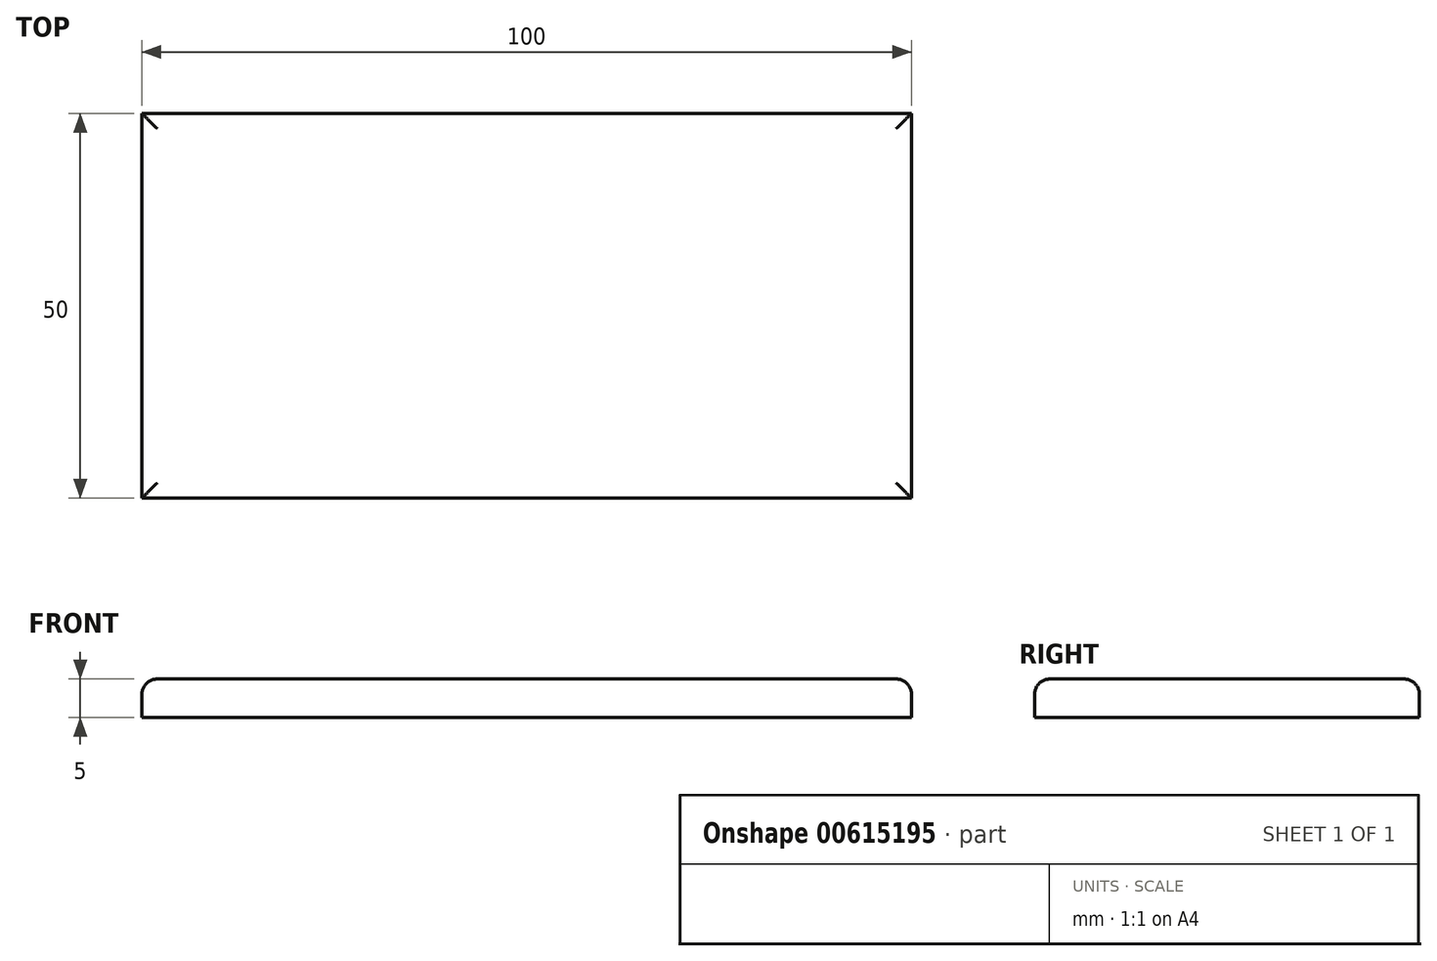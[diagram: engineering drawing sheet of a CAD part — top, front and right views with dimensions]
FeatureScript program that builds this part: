
annotation { "Feature Type Name" : "Feature", "Feature Type Description" : "" }
export const myFeature = defineFeature(function(context is Context, id is Id, definition is map)
    precondition{}
    {
        {
            var Q0;
            Q0=qCreatedBy(makeId("Top.planeOp"),FACE);
            var sketch = newSketch(context, id + "F0", { "sketchPlane" : qUnion([Q0])});
            skLineSegment(sketch, "E0.bottom", {"start": v(0, 0) * mm, "end": v(100, 0) * mm});
            skLineSegment(sketch, "E0.top", {"start": v(0, 50) * mm, "end": v(100, 50) * mm});
            skLineSegment(sketch, "E0.left", {"start": v(0, 0) * mm, "end": v(0, 50) * mm});
            skLineSegment(sketch, "E0.right", {"start": v(100, 0) * mm, "end": v(100, 50) * mm});
            skSolve(sketch);
        }
        {
            var Q0;
            Q0 = qSketchRegion(id + "F0", true);
            extrude(context, id + "F1", {"entities" : qUnion([Q0]), "depth" : 5 * mm, "offsetDistance" : 25 * mm});
        }
        {
            var Q0;
            Q0=makeQuery(id+"F1.opExtrude","CAP_EDGE",EDGE,{"disambiguationData":[OSD([sQuery(id+"F0.wireOp",EDGE,"E0.left")])],"isStart":false});
            var Q1;
            Q1=makeQuery(id+"F1.opExtrude","CAP_EDGE",EDGE,{"disambiguationData":[OSD([sQuery(id+"F0.wireOp",EDGE,"E0.bottom")])],"isStart":false});
            var Q2;
            Q2=makeQuery(id+"F1.opExtrude","CAP_EDGE",EDGE,{"disambiguationData":[OSD([sQuery(id+"F0.wireOp",EDGE,"E0.top")])],"isStart":false});
            var Q3;
            Q3=makeQuery(id+"F1.opExtrude","CAP_EDGE",EDGE,{"disambiguationData":[OSD([sQuery(id+"F0.wireOp",EDGE,"E0.right")])],"isStart":false});
            fillet(context, id + "F2", {"entities" : qUnion([Q0, Q1, Q2, Q3]), "radius" : 2 * mm, "tangentPropagation" : true, "allowEdgeOverflow" : false});
        }
    });
